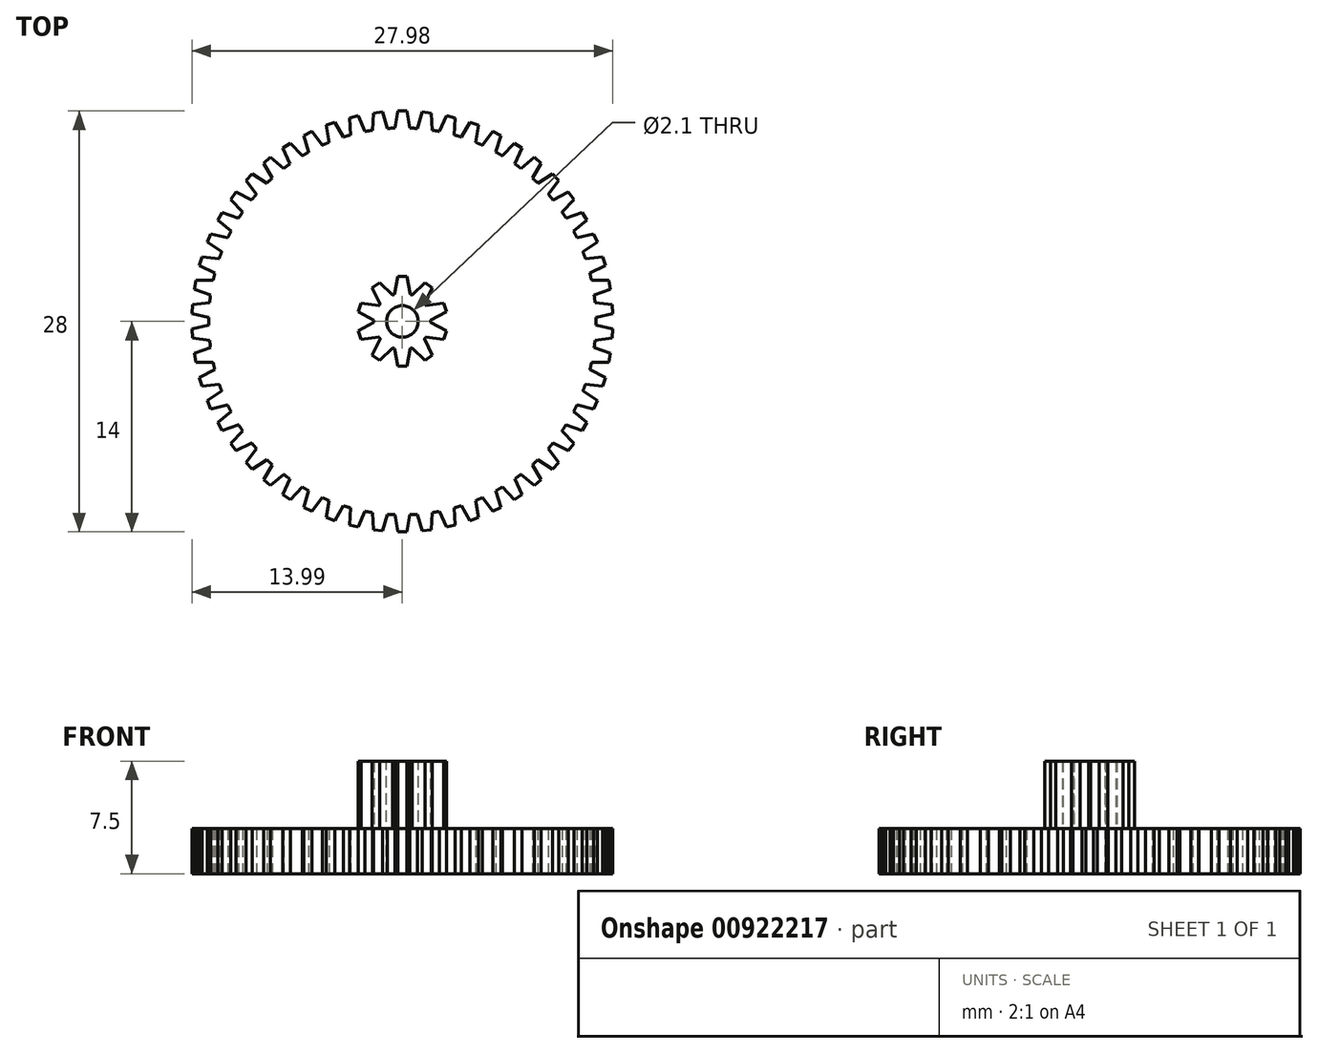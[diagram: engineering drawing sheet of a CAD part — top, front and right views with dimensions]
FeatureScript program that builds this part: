
annotation { "Feature Type Name" : "Feature", "Feature Type Description" : "" }
export const myFeature = defineFeature(function(context is Context, id is Id, definition is map)
    precondition{}
    {
        {
            var Q0;
            Q0=qCreatedBy(makeId("Top.planeOp"),FACE);
            var sketch = newSketch(context, id + "F0", { "sketchPlane" : qUnion([Q0])});
            skCircle(sketch, "E0", {"center": v(0, 0) * mm, "radius": 13.5 * mm, "construction": true});
            skCircle(sketch, "E1", {"center": v(0, 0) * mm, "radius": 14 * mm, "construction": true});
            skCircle(sketch, "E2", {"center": v(0, 0) * mm, "radius": 12.88 * mm});
            skLineSegment(sketch, "E3", {"start": v(0, 12.88) * mm, "end": v(0.5, 12.88) * mm, "construction": true});
            skLineSegment(sketch, "E4", {"start": v(0, 12.88) * mm, "end": v(-0.5, 12.88) * mm, "construction": true});
            skLineSegment(sketch, "E5", {"start": v(-1.53, 7.02) * mm, "end": v(-0.5, 12.87) * mm, "construction": true});
            skLineSegment(sketch, "E6", {"start": v(1.53, 7.03) * mm, "end": v(0.3, 14) * mm, "construction": true});
            skLineSegment(sketch, "E7", {"start": v(-1.53, 7.03) * mm, "end": v(-0.3, 14) * mm});
            skLineSegment(sketch, "E8", {"start": v(0.3, 14) * mm, "end": v(-0.3, 14) * mm});
            skLineSegment(sketch, "E9", {"start": v(0.3, 14) * mm, "end": v(0.5, 12.87) * mm});
            skLineSegment(sketch, "E10.1.0", {"start": v(-2.34, 6.8) * mm, "end": v(-1.93, 13.87) * mm});
            skLineSegment(sketch, "E10.1.1", {"start": v(-1.32, 13.94) * mm, "end": v(-1.93, 13.87) * mm});
            skLineSegment(sketch, "E10.1.2", {"start": v(-1.32, 13.94) * mm, "end": v(-1, 12.84) * mm});
            skLineSegment(sketch, "E10.2.0", {"start": v(-3.11, 6.5) * mm, "end": v(-3.52, 13.55) * mm});
            skLineSegment(sketch, "E10.2.1", {"start": v(-2.93, 13.69) * mm, "end": v(-3.52, 13.55) * mm});
            skLineSegment(sketch, "E10.2.2", {"start": v(-2.93, 13.69) * mm, "end": v(-2.48, 12.63) * mm});
            skLineSegment(sketch, "E11.1.3.0", {"start": v(-3.84, 6.09) * mm, "end": v(-5.07, 13.05) * mm});
            skLineSegment(sketch, "E11.3.3.0", {"start": v(-4.5, 13.26) * mm, "end": v(-5.07, 13.05) * mm});
            skLineSegment(sketch, "E11.6.3.0", {"start": v(-4.5, 13.26) * mm, "end": v(-3.93, 12.26) * mm});
            skLineSegment(sketch, "E11.1.4.0", {"start": v(-4.52, 5.6) * mm, "end": v(-6.55, 12.37) * mm});
            skLineSegment(sketch, "E11.3.4.0", {"start": v(-6.01, 12.64) * mm, "end": v(-6.55, 12.37) * mm});
            skLineSegment(sketch, "E11.6.4.0", {"start": v(-6.01, 12.64) * mm, "end": v(-5.33, 11.72) * mm});
            skLineSegment(sketch, "E11.1.5.0", {"start": v(-5.14, 5.04) * mm, "end": v(-7.94, 11.53) * mm});
            skLineSegment(sketch, "E11.3.5.0", {"start": v(-7.44, 11.86) * mm, "end": v(-7.94, 11.53) * mm});
            skLineSegment(sketch, "E11.6.5.0", {"start": v(-7.44, 11.86) * mm, "end": v(-6.65, 11.02) * mm});
            skLineSegment(sketch, "E11.1.6.0", {"start": v(-5.7, 4.4) * mm, "end": v(-9.23, 10.53) * mm});
            skLineSegment(sketch, "E11.3.6.0", {"start": v(-8.77, 10.92) * mm, "end": v(-9.23, 10.53) * mm});
            skLineSegment(sketch, "E11.6.6.0", {"start": v(-8.77, 10.92) * mm, "end": v(-7.89, 10.18) * mm});
            skLineSegment(sketch, "E11.1.7.0", {"start": v(-6.17, 3.71) * mm, "end": v(-10.39, 9.39) * mm});
            skLineSegment(sketch, "E11.3.7.0", {"start": v(-9.97, 9.82) * mm, "end": v(-10.39, 9.39) * mm});
            skLineSegment(sketch, "E11.6.7.0", {"start": v(-9.97, 9.82) * mm, "end": v(-9.01, 9.2) * mm});
            skLineSegment(sketch, "E11.1.8.0", {"start": v(-6.56, 2.97) * mm, "end": v(-11.4, 8.12) * mm});
            skLineSegment(sketch, "E11.3.8.0", {"start": v(-11.05, 8.6) * mm, "end": v(-11.4, 8.12) * mm});
            skLineSegment(sketch, "E11.6.8.0", {"start": v(-11.05, 8.6) * mm, "end": v(-10.02, 8.09) * mm});
            skLineSegment(sketch, "E11.1.9.0", {"start": v(-6.86, 2.2) * mm, "end": v(-12.27, 6.74) * mm});
            skLineSegment(sketch, "E11.3.9.0", {"start": v(-11.97, 7.26) * mm, "end": v(-12.27, 6.74) * mm});
            skLineSegment(sketch, "E11.6.9.0", {"start": v(-11.97, 7.26) * mm, "end": v(-10.9, 6.87) * mm});
            skLineSegment(sketch, "E11.1.10.0", {"start": v(-7.06, 1.38) * mm, "end": v(-12.97, 5.27) * mm});
            skLineSegment(sketch, "E11.3.10.0", {"start": v(-12.73, 5.82) * mm, "end": v(-12.97, 5.27) * mm});
            skLineSegment(sketch, "E11.6.10.0", {"start": v(-12.73, 5.82) * mm, "end": v(-11.61, 5.56) * mm});
            skLineSegment(sketch, "E11.1.11.0", {"start": v(-7.18, 0.55) * mm, "end": v(-13.5, 3.72) * mm});
            skLineSegment(sketch, "E11.3.11.0", {"start": v(-13.32, 4.3) * mm, "end": v(-13.5, 3.72) * mm});
            skLineSegment(sketch, "E11.6.11.0", {"start": v(-13.32, 4.3) * mm, "end": v(-12.18, 4.17) * mm});
            skLineSegment(sketch, "E11.1.12.0", {"start": v(-7.2, -0.29) * mm, "end": v(-13.84, 2.13) * mm});
            skLineSegment(sketch, "E11.3.12.0", {"start": v(-13.73, 2.73) * mm, "end": v(-13.84, 2.13) * mm});
            skLineSegment(sketch, "E11.6.12.0", {"start": v(-13.73, 2.73) * mm, "end": v(-12.58, 2.73) * mm});
            skLineSegment(sketch, "E11.1.13.0", {"start": v(-7.11, -1.12) * mm, "end": v(-14, 0.51) * mm});
            skLineSegment(sketch, "E11.3.13.0", {"start": v(-13.96, 1.12) * mm, "end": v(-14, 0.51) * mm});
            skLineSegment(sketch, "E11.6.13.0", {"start": v(-13.96, 1.12) * mm, "end": v(-12.81, 1.25) * mm});
            skLineSegment(sketch, "E11.1.14.0", {"start": v(-6.93, -1.94) * mm, "end": v(-13.96, -1.12) * mm});
            skLineSegment(sketch, "E11.3.14.0", {"start": v(-14, -0.51) * mm, "end": v(-13.96, -1.12) * mm});
            skLineSegment(sketch, "E11.6.14.0", {"start": v(-14, -0.51) * mm, "end": v(-12.87, -0.25) * mm});
            skLineSegment(sketch, "E11.1.15.0", {"start": v(-6.66, -2.73) * mm, "end": v(-13.73, -2.73) * mm});
            skLineSegment(sketch, "E11.3.15.0", {"start": v(-13.84, -2.13) * mm, "end": v(-13.73, -2.73) * mm});
            skLineSegment(sketch, "E11.6.15.0", {"start": v(-13.84, -2.13) * mm, "end": v(-12.76, -1.74) * mm});
            skLineSegment(sketch, "E11.1.16.0", {"start": v(-6.3, -3.48) * mm, "end": v(-13.32, -4.3) * mm});
            skLineSegment(sketch, "E11.3.16.0", {"start": v(-13.5, -3.72) * mm, "end": v(-13.32, -4.3) * mm});
            skLineSegment(sketch, "E11.6.16.0", {"start": v(-13.5, -3.72) * mm, "end": v(-12.47, -3.2) * mm});
            skLineSegment(sketch, "E11.1.17.0", {"start": v(-5.85, -4.2) * mm, "end": v(-12.73, -5.82) * mm});
            skLineSegment(sketch, "E11.3.17.0", {"start": v(-12.97, -5.27) * mm, "end": v(-12.73, -5.82) * mm});
            skLineSegment(sketch, "E11.6.17.0", {"start": v(-12.97, -5.27) * mm, "end": v(-12.01, -4.63) * mm});
            skLineSegment(sketch, "E11.1.18.0", {"start": v(-5.33, -4.84) * mm, "end": v(-11.97, -7.26) * mm});
            skLineSegment(sketch, "E11.3.18.0", {"start": v(-12.27, -6.74) * mm, "end": v(-11.97, -7.26) * mm});
            skLineSegment(sketch, "E11.6.18.0", {"start": v(-12.27, -6.74) * mm, "end": v(-11.4, -6) * mm});
            skLineSegment(sketch, "E11.1.19.0", {"start": v(-4.73, -5.43) * mm, "end": v(-11.05, -8.6) * mm});
            skLineSegment(sketch, "E11.3.19.0", {"start": v(-11.4, -8.12) * mm, "end": v(-11.05, -8.6) * mm});
            skLineSegment(sketch, "E11.6.19.0", {"start": v(-11.4, -8.12) * mm, "end": v(-10.62, -7.28) * mm});
            skLineSegment(sketch, "E11.1.20.0", {"start": v(-4.07, -5.94) * mm, "end": v(-9.97, -9.82) * mm});
            skLineSegment(sketch, "E11.3.20.0", {"start": v(-10.39, -9.39) * mm, "end": v(-9.97, -9.82) * mm});
            skLineSegment(sketch, "E11.6.20.0", {"start": v(-10.39, -9.39) * mm, "end": v(-9.7, -8.46) * mm});
            skLineSegment(sketch, "E11.1.21.0", {"start": v(-3.35, -6.37) * mm, "end": v(-8.77, -10.92) * mm});
            skLineSegment(sketch, "E11.3.21.0", {"start": v(-9.23, -10.53) * mm, "end": v(-8.77, -10.92) * mm});
            skLineSegment(sketch, "E11.6.21.0", {"start": v(-9.23, -10.53) * mm, "end": v(-8.65, -9.53) * mm});
            skLineSegment(sketch, "E11.1.22.0", {"start": v(-2.59, -6.72) * mm, "end": v(-7.44, -11.86) * mm});
            skLineSegment(sketch, "E11.3.22.0", {"start": v(-7.94, -11.53) * mm, "end": v(-7.44, -11.86) * mm});
            skLineSegment(sketch, "E11.6.22.0", {"start": v(-7.94, -11.53) * mm, "end": v(-7.49, -10.47) * mm});
            skLineSegment(sketch, "E11.1.23.0", {"start": v(-1.79, -6.97) * mm, "end": v(-6.01, -12.64) * mm});
            skLineSegment(sketch, "E11.3.23.0", {"start": v(-6.55, -12.37) * mm, "end": v(-6.01, -12.64) * mm});
            skLineSegment(sketch, "E11.6.23.0", {"start": v(-6.55, -12.37) * mm, "end": v(-6.22, -11.27) * mm});
            skLineSegment(sketch, "E11.1.24.0", {"start": v(-0.97, -7.13) * mm, "end": v(-4.5, -13.26) * mm});
            skLineSegment(sketch, "E11.3.24.0", {"start": v(-5.07, -13.05) * mm, "end": v(-4.5, -13.26) * mm});
            skLineSegment(sketch, "E11.6.24.0", {"start": v(-5.07, -13.05) * mm, "end": v(-4.87, -11.92) * mm});
            skLineSegment(sketch, "E11.1.25.0", {"start": v(-0.13, -7.2) * mm, "end": v(-2.93, -13.69) * mm});
            skLineSegment(sketch, "E11.3.25.0", {"start": v(-3.52, -13.55) * mm, "end": v(-2.93, -13.69) * mm});
            skLineSegment(sketch, "E11.6.25.0", {"start": v(-3.52, -13.55) * mm, "end": v(-3.46, -12.4) * mm});
            skLineSegment(sketch, "E11.1.26.0", {"start": v(0.7, -7.16) * mm, "end": v(-1.32, -13.94) * mm});
            skLineSegment(sketch, "E11.3.26.0", {"start": v(-1.93, -13.87) * mm, "end": v(-1.32, -13.94) * mm});
            skLineSegment(sketch, "E11.6.26.0", {"start": v(-1.93, -13.87) * mm, "end": v(-2, -12.72) * mm});
            skLineSegment(sketch, "E11.1.27.0", {"start": v(1.53, -7.03) * mm, "end": v(0.3, -14) * mm});
            skLineSegment(sketch, "E11.3.27.0", {"start": v(-0.3, -14) * mm, "end": v(0.3, -14) * mm});
            skLineSegment(sketch, "E11.6.27.0", {"start": v(-0.3, -14) * mm, "end": v(-0.5, -12.87) * mm});
            skLineSegment(sketch, "E11.1.28.0", {"start": v(2.34, -6.8) * mm, "end": v(1.93, -13.87) * mm});
            skLineSegment(sketch, "E11.3.28.0", {"start": v(1.32, -13.94) * mm, "end": v(1.93, -13.87) * mm});
            skLineSegment(sketch, "E11.6.28.0", {"start": v(1.32, -13.94) * mm, "end": v(1, -12.84) * mm});
            skLineSegment(sketch, "E11.1.29.0", {"start": v(3.11, -6.5) * mm, "end": v(3.52, -13.55) * mm});
            skLineSegment(sketch, "E11.3.29.0", {"start": v(2.93, -13.69) * mm, "end": v(3.52, -13.55) * mm});
            skLineSegment(sketch, "E11.6.29.0", {"start": v(2.93, -13.69) * mm, "end": v(2.48, -12.63) * mm});
            skLineSegment(sketch, "E12.1.30.0", {"start": v(3.84, -6.09) * mm, "end": v(5.07, -13.05) * mm});
            skLineSegment(sketch, "E12.3.30.0", {"start": v(4.5, -13.26) * mm, "end": v(5.07, -13.05) * mm});
            skLineSegment(sketch, "E12.6.30.0", {"start": v(4.5, -13.26) * mm, "end": v(3.93, -12.26) * mm});
            skLineSegment(sketch, "E12.1.31.0", {"start": v(4.52, -5.6) * mm, "end": v(6.55, -12.37) * mm});
            skLineSegment(sketch, "E12.3.31.0", {"start": v(6.01, -12.64) * mm, "end": v(6.55, -12.37) * mm});
            skLineSegment(sketch, "E12.6.31.0", {"start": v(6.01, -12.64) * mm, "end": v(5.33, -11.72) * mm});
            skLineSegment(sketch, "E12.1.32.0", {"start": v(5.14, -5.04) * mm, "end": v(7.94, -11.53) * mm});
            skLineSegment(sketch, "E12.3.32.0", {"start": v(7.44, -11.86) * mm, "end": v(7.94, -11.53) * mm});
            skLineSegment(sketch, "E12.6.32.0", {"start": v(7.44, -11.86) * mm, "end": v(6.65, -11.02) * mm});
            skLineSegment(sketch, "E12.1.33.0", {"start": v(5.7, -4.4) * mm, "end": v(9.23, -10.53) * mm});
            skLineSegment(sketch, "E12.3.33.0", {"start": v(8.77, -10.92) * mm, "end": v(9.23, -10.53) * mm});
            skLineSegment(sketch, "E12.6.33.0", {"start": v(8.77, -10.92) * mm, "end": v(7.89, -10.18) * mm});
            skLineSegment(sketch, "E12.1.34.0", {"start": v(6.17, -3.71) * mm, "end": v(10.39, -9.39) * mm});
            skLineSegment(sketch, "E12.3.34.0", {"start": v(9.97, -9.82) * mm, "end": v(10.39, -9.39) * mm});
            skLineSegment(sketch, "E12.6.34.0", {"start": v(9.97, -9.82) * mm, "end": v(9.01, -9.2) * mm});
            skLineSegment(sketch, "E12.1.35.0", {"start": v(6.56, -2.97) * mm, "end": v(11.4, -8.12) * mm});
            skLineSegment(sketch, "E12.3.35.0", {"start": v(11.05, -8.6) * mm, "end": v(11.4, -8.12) * mm});
            skLineSegment(sketch, "E12.6.35.0", {"start": v(11.05, -8.6) * mm, "end": v(10.02, -8.09) * mm});
            skLineSegment(sketch, "E12.1.36.0", {"start": v(6.86, -2.2) * mm, "end": v(12.27, -6.74) * mm});
            skLineSegment(sketch, "E12.3.36.0", {"start": v(11.97, -7.26) * mm, "end": v(12.27, -6.74) * mm});
            skLineSegment(sketch, "E12.6.36.0", {"start": v(11.97, -7.26) * mm, "end": v(10.9, -6.87) * mm});
            skLineSegment(sketch, "E12.1.37.0", {"start": v(7.06, -1.38) * mm, "end": v(12.97, -5.27) * mm});
            skLineSegment(sketch, "E12.3.37.0", {"start": v(12.73, -5.82) * mm, "end": v(12.97, -5.27) * mm});
            skLineSegment(sketch, "E12.6.37.0", {"start": v(12.73, -5.82) * mm, "end": v(11.61, -5.56) * mm});
            skLineSegment(sketch, "E12.1.38.0", {"start": v(7.18, -0.55) * mm, "end": v(13.5, -3.72) * mm});
            skLineSegment(sketch, "E12.3.38.0", {"start": v(13.32, -4.3) * mm, "end": v(13.5, -3.72) * mm});
            skLineSegment(sketch, "E12.6.38.0", {"start": v(13.32, -4.3) * mm, "end": v(12.18, -4.17) * mm});
            skLineSegment(sketch, "E12.1.39.0", {"start": v(7.2, 0.29) * mm, "end": v(13.84, -2.13) * mm});
            skLineSegment(sketch, "E12.3.39.0", {"start": v(13.73, -2.73) * mm, "end": v(13.84, -2.13) * mm});
            skLineSegment(sketch, "E12.6.39.0", {"start": v(13.73, -2.73) * mm, "end": v(12.58, -2.73) * mm});
            skLineSegment(sketch, "E12.1.40.0", {"start": v(7.11, 1.12) * mm, "end": v(14, -0.51) * mm});
            skLineSegment(sketch, "E12.3.40.0", {"start": v(13.96, -1.12) * mm, "end": v(14, -0.51) * mm});
            skLineSegment(sketch, "E12.6.40.0", {"start": v(13.96, -1.12) * mm, "end": v(12.81, -1.25) * mm});
            skLineSegment(sketch, "E12.1.41.0", {"start": v(6.93, 1.94) * mm, "end": v(13.96, 1.12) * mm});
            skLineSegment(sketch, "E12.3.41.0", {"start": v(14, 0.51) * mm, "end": v(13.96, 1.12) * mm});
            skLineSegment(sketch, "E12.6.41.0", {"start": v(14, 0.51) * mm, "end": v(12.87, 0.25) * mm});
            skLineSegment(sketch, "E13.1.42.0", {"start": v(6.66, 2.73) * mm, "end": v(13.73, 2.73) * mm});
            skLineSegment(sketch, "E13.3.42.0", {"start": v(13.84, 2.13) * mm, "end": v(13.73, 2.73) * mm});
            skLineSegment(sketch, "E13.6.42.0", {"start": v(13.84, 2.13) * mm, "end": v(12.76, 1.74) * mm});
            skLineSegment(sketch, "E13.1.43.0", {"start": v(6.3, 3.48) * mm, "end": v(13.32, 4.3) * mm});
            skLineSegment(sketch, "E13.3.43.0", {"start": v(13.5, 3.72) * mm, "end": v(13.32, 4.3) * mm});
            skLineSegment(sketch, "E13.6.43.0", {"start": v(13.5, 3.72) * mm, "end": v(12.47, 3.2) * mm});
            skLineSegment(sketch, "E13.1.44.0", {"start": v(5.85, 4.2) * mm, "end": v(12.73, 5.82) * mm});
            skLineSegment(sketch, "E13.3.44.0", {"start": v(12.97, 5.27) * mm, "end": v(12.73, 5.82) * mm});
            skLineSegment(sketch, "E13.6.44.0", {"start": v(12.97, 5.27) * mm, "end": v(12.01, 4.63) * mm});
            skLineSegment(sketch, "E13.1.45.0", {"start": v(5.33, 4.84) * mm, "end": v(11.97, 7.26) * mm});
            skLineSegment(sketch, "E13.3.45.0", {"start": v(12.27, 6.74) * mm, "end": v(11.97, 7.26) * mm});
            skLineSegment(sketch, "E13.6.45.0", {"start": v(12.27, 6.74) * mm, "end": v(11.4, 6) * mm});
            skLineSegment(sketch, "E13.1.46.0", {"start": v(4.73, 5.43) * mm, "end": v(11.05, 8.6) * mm});
            skLineSegment(sketch, "E13.3.46.0", {"start": v(11.4, 8.12) * mm, "end": v(11.05, 8.6) * mm});
            skLineSegment(sketch, "E13.6.46.0", {"start": v(11.4, 8.12) * mm, "end": v(10.62, 7.28) * mm});
            skLineSegment(sketch, "E13.1.47.0", {"start": v(4.07, 5.94) * mm, "end": v(9.97, 9.82) * mm});
            skLineSegment(sketch, "E13.3.47.0", {"start": v(10.39, 9.39) * mm, "end": v(9.97, 9.82) * mm});
            skLineSegment(sketch, "E13.6.47.0", {"start": v(10.39, 9.39) * mm, "end": v(9.7, 8.46) * mm});
            skLineSegment(sketch, "E14.1.48.0", {"start": v(3.35, 6.37) * mm, "end": v(8.77, 10.92) * mm});
            skLineSegment(sketch, "E14.3.48.0", {"start": v(9.23, 10.53) * mm, "end": v(8.77, 10.92) * mm});
            skLineSegment(sketch, "E14.6.48.0", {"start": v(9.23, 10.53) * mm, "end": v(8.65, 9.53) * mm});
            skLineSegment(sketch, "E14.1.49.0", {"start": v(2.59, 6.72) * mm, "end": v(7.44, 11.86) * mm});
            skLineSegment(sketch, "E14.3.49.0", {"start": v(7.94, 11.53) * mm, "end": v(7.44, 11.86) * mm});
            skLineSegment(sketch, "E14.6.49.0", {"start": v(7.94, 11.53) * mm, "end": v(7.49, 10.47) * mm});
            skLineSegment(sketch, "E14.1.50.0", {"start": v(1.79, 6.97) * mm, "end": v(6.01, 12.64) * mm});
            skLineSegment(sketch, "E14.3.50.0", {"start": v(6.55, 12.37) * mm, "end": v(6.01, 12.64) * mm});
            skLineSegment(sketch, "E14.6.50.0", {"start": v(6.55, 12.37) * mm, "end": v(6.22, 11.27) * mm});
            skLineSegment(sketch, "E14.1.51.0", {"start": v(0.97, 7.13) * mm, "end": v(4.5, 13.26) * mm});
            skLineSegment(sketch, "E14.3.51.0", {"start": v(5.07, 13.05) * mm, "end": v(4.5, 13.26) * mm});
            skLineSegment(sketch, "E14.6.51.0", {"start": v(5.07, 13.05) * mm, "end": v(4.87, 11.92) * mm});
            skLineSegment(sketch, "E14.1.52.0", {"start": v(0.13, 7.2) * mm, "end": v(2.93, 13.69) * mm});
            skLineSegment(sketch, "E14.3.52.0", {"start": v(3.52, 13.55) * mm, "end": v(2.93, 13.69) * mm});
            skLineSegment(sketch, "E14.6.52.0", {"start": v(3.52, 13.55) * mm, "end": v(3.46, 12.4) * mm});
            skLineSegment(sketch, "E14.1.53.0", {"start": v(-0.7, 7.16) * mm, "end": v(1.32, 13.94) * mm});
            skLineSegment(sketch, "E14.3.53.0", {"start": v(1.93, 13.87) * mm, "end": v(1.32, 13.94) * mm});
            skLineSegment(sketch, "E14.6.53.0", {"start": v(1.93, 13.87) * mm, "end": v(2, 12.72) * mm});
            skSolve(sketch);
        }
        {
            var Q0;
            Q0=qSketchRegion(id+"F0",true);
            extrude(context, id + "F1", {"entities" : qUnion([Q0]), "depth" : 3 * mm, "offsetDistance" : 25 * mm});
        }
        {
            var Q0;
            Q0=makeQuery(id+"F1.opExtrude","CAP_FACE",FACE,{"disambiguationData":[OSD([sQuery(id+"F0.wireOp",EDGE,"E2"),sQuery(id+"F0.wireOp",EDGE,"E7"),sQuery(id+"F0.wireOp",EDGE,"E8"),sQuery(id+"F0.wireOp",EDGE,"E9"),sQuery(id+"F0.wireOp",EDGE,"E10.1.0"),sQuery(id+"F0.wireOp",EDGE,"E10.1.1"),sQuery(id+"F0.wireOp",EDGE,"E10.1.2"),sQuery(id+"F0.wireOp",EDGE,"E10.2.0"),sQuery(id+"F0.wireOp",EDGE,"E10.2.1"),sQuery(id+"F0.wireOp",EDGE,"E10.2.2"),sQuery(id+"F0.wireOp",EDGE,"E11.1.3.0"),sQuery(id+"F0.wireOp",EDGE,"E11.3.3.0"),sQuery(id+"F0.wireOp",EDGE,"E11.6.3.0"),sQuery(id+"F0.wireOp",EDGE,"E11.1.4.0"),sQuery(id+"F0.wireOp",EDGE,"E11.3.4.0"),sQuery(id+"F0.wireOp",EDGE,"E11.6.4.0"),sQuery(id+"F0.wireOp",EDGE,"E11.1.5.0"),sQuery(id+"F0.wireOp",EDGE,"E11.3.5.0"),sQuery(id+"F0.wireOp",EDGE,"E11.6.5.0"),sQuery(id+"F0.wireOp",EDGE,"E11.1.6.0"),sQuery(id+"F0.wireOp",EDGE,"E11.3.6.0"),sQuery(id+"F0.wireOp",EDGE,"E11.6.6.0"),sQuery(id+"F0.wireOp",EDGE,"E11.1.7.0"),sQuery(id+"F0.wireOp",EDGE,"E11.3.7.0"),sQuery(id+"F0.wireOp",EDGE,"E11.6.7.0"),sQuery(id+"F0.wireOp",EDGE,"E11.1.8.0"),sQuery(id+"F0.wireOp",EDGE,"E11.3.8.0"),sQuery(id+"F0.wireOp",EDGE,"E11.6.8.0"),sQuery(id+"F0.wireOp",EDGE,"E11.1.9.0"),sQuery(id+"F0.wireOp",EDGE,"E11.3.9.0"),sQuery(id+"F0.wireOp",EDGE,"E11.6.9.0"),sQuery(id+"F0.wireOp",EDGE,"E11.1.10.0"),sQuery(id+"F0.wireOp",EDGE,"E11.3.10.0"),sQuery(id+"F0.wireOp",EDGE,"E11.6.10.0"),sQuery(id+"F0.wireOp",EDGE,"E11.1.11.0"),sQuery(id+"F0.wireOp",EDGE,"E11.3.11.0"),sQuery(id+"F0.wireOp",EDGE,"E11.6.11.0"),sQuery(id+"F0.wireOp",EDGE,"E11.1.12.0"),sQuery(id+"F0.wireOp",EDGE,"E11.3.12.0"),sQuery(id+"F0.wireOp",EDGE,"E11.6.12.0"),sQuery(id+"F0.wireOp",EDGE,"E11.1.13.0"),sQuery(id+"F0.wireOp",EDGE,"E11.3.13.0"),sQuery(id+"F0.wireOp",EDGE,"E11.6.13.0"),sQuery(id+"F0.wireOp",EDGE,"E11.1.14.0"),sQuery(id+"F0.wireOp",EDGE,"E11.3.14.0"),sQuery(id+"F0.wireOp",EDGE,"E11.6.14.0"),sQuery(id+"F0.wireOp",EDGE,"E11.1.15.0"),sQuery(id+"F0.wireOp",EDGE,"E11.3.15.0"),sQuery(id+"F0.wireOp",EDGE,"E11.6.15.0"),sQuery(id+"F0.wireOp",EDGE,"E11.1.16.0"),sQuery(id+"F0.wireOp",EDGE,"E11.3.16.0"),sQuery(id+"F0.wireOp",EDGE,"E11.6.16.0"),sQuery(id+"F0.wireOp",EDGE,"E11.1.17.0"),sQuery(id+"F0.wireOp",EDGE,"E11.3.17.0"),sQuery(id+"F0.wireOp",EDGE,"E11.6.17.0"),sQuery(id+"F0.wireOp",EDGE,"E11.1.18.0"),sQuery(id+"F0.wireOp",EDGE,"E11.3.18.0"),sQuery(id+"F0.wireOp",EDGE,"E11.6.18.0"),sQuery(id+"F0.wireOp",EDGE,"E11.1.19.0"),sQuery(id+"F0.wireOp",EDGE,"E11.3.19.0"),sQuery(id+"F0.wireOp",EDGE,"E11.6.19.0"),sQuery(id+"F0.wireOp",EDGE,"E11.1.20.0"),sQuery(id+"F0.wireOp",EDGE,"E11.3.20.0"),sQuery(id+"F0.wireOp",EDGE,"E11.6.20.0"),sQuery(id+"F0.wireOp",EDGE,"E11.1.21.0"),sQuery(id+"F0.wireOp",EDGE,"E11.3.21.0"),sQuery(id+"F0.wireOp",EDGE,"E11.6.21.0"),sQuery(id+"F0.wireOp",EDGE,"E11.1.22.0"),sQuery(id+"F0.wireOp",EDGE,"E11.3.22.0"),sQuery(id+"F0.wireOp",EDGE,"E11.6.22.0"),sQuery(id+"F0.wireOp",EDGE,"E11.1.23.0"),sQuery(id+"F0.wireOp",EDGE,"E11.3.23.0"),sQuery(id+"F0.wireOp",EDGE,"E11.6.23.0"),sQuery(id+"F0.wireOp",EDGE,"E11.1.24.0"),sQuery(id+"F0.wireOp",EDGE,"E11.3.24.0"),sQuery(id+"F0.wireOp",EDGE,"E11.6.24.0"),sQuery(id+"F0.wireOp",EDGE,"E11.1.25.0"),sQuery(id+"F0.wireOp",EDGE,"E11.3.25.0"),sQuery(id+"F0.wireOp",EDGE,"E11.6.25.0"),sQuery(id+"F0.wireOp",EDGE,"E11.1.26.0"),sQuery(id+"F0.wireOp",EDGE,"E11.3.26.0"),sQuery(id+"F0.wireOp",EDGE,"E11.6.26.0"),sQuery(id+"F0.wireOp",EDGE,"E11.1.27.0"),sQuery(id+"F0.wireOp",EDGE,"E11.3.27.0"),sQuery(id+"F0.wireOp",EDGE,"E11.6.27.0"),sQuery(id+"F0.wireOp",EDGE,"E11.1.28.0"),sQuery(id+"F0.wireOp",EDGE,"E11.3.28.0"),sQuery(id+"F0.wireOp",EDGE,"E11.6.28.0"),sQuery(id+"F0.wireOp",EDGE,"E11.1.29.0"),sQuery(id+"F0.wireOp",EDGE,"E11.3.29.0"),sQuery(id+"F0.wireOp",EDGE,"E11.6.29.0")])],"isStart":false});
            var sketch = newSketch(context, id + "F2", { "sketchPlane" : qUnion([Q0])});
            skCircle(sketch, "E15", {"center": v(0, 0) * mm, "radius": 2.5 * mm, "construction": true});
            skCircle(sketch, "E16", {"center": v(0, 0) * mm, "radius": 3 * mm, "construction": true});
            skCircle(sketch, "E17", {"center": v(0, 0) * mm, "radius": 1.88 * mm});
            skLineSegment(sketch, "E18", {"start": v(0, 1.88) * mm, "end": v(0.5, 1.88) * mm, "construction": true});
            skLineSegment(sketch, "E19", {"start": v(0, 1.88) * mm, "end": v(-0.5, 1.88) * mm, "construction": true});
            skLineSegment(sketch, "E20", {"start": v(-0.51, 1.8) * mm, "end": v(-0.3, 2.98) * mm, "construction": true});
            skLineSegment(sketch, "E21", {"start": v(0.51, 1.8) * mm, "end": v(0.3, 2.98) * mm, "construction": true});
            skLineSegment(sketch, "E22", {"start": v(-0.51, 1.8) * mm, "end": v(-0.3, 2.98) * mm});
            skLineSegment(sketch, "E23", {"start": v(0.3, 2.98) * mm, "end": v(-0.3, 2.98) * mm});
            skLineSegment(sketch, "E24", {"start": v(0.3, 2.98) * mm, "end": v(0.51, 1.8) * mm});
            skLineSegment(sketch, "E25.1.0", {"start": v(-1.47, 1.16) * mm, "end": v(-2, 2.24) * mm});
            skLineSegment(sketch, "E25.1.1", {"start": v(-1.5, 2.6) * mm, "end": v(-2, 2.24) * mm});
            skLineSegment(sketch, "E25.1.2", {"start": v(-1.5, 2.6) * mm, "end": v(-0.65, 1.76) * mm});
            skLineSegment(sketch, "E25.2.0", {"start": v(-1.87, 0.07) * mm, "end": v(-2.93, 0.63) * mm});
            skLineSegment(sketch, "E25.2.1", {"start": v(-2.74, 1.21) * mm, "end": v(-2.93, 0.63) * mm});
            skLineSegment(sketch, "E25.2.2", {"start": v(-2.74, 1.21) * mm, "end": v(-1.56, 1.04) * mm});
            skLineSegment(sketch, "E26.1.3.0", {"start": v(-1.56, -1.04) * mm, "end": v(-2.74, -1.21) * mm});
            skLineSegment(sketch, "E26.3.3.0", {"start": v(-2.93, -0.63) * mm, "end": v(-2.74, -1.21) * mm});
            skLineSegment(sketch, "E26.6.3.0", {"start": v(-2.93, -0.63) * mm, "end": v(-1.87, -0.07) * mm});
            skLineSegment(sketch, "E26.1.4.0", {"start": v(-0.65, -1.76) * mm, "end": v(-1.5, -2.6) * mm});
            skLineSegment(sketch, "E26.3.4.0", {"start": v(-2, -2.24) * mm, "end": v(-1.5, -2.6) * mm});
            skLineSegment(sketch, "E26.6.4.0", {"start": v(-2, -2.24) * mm, "end": v(-1.47, -1.16) * mm});
            skLineSegment(sketch, "E26.1.5.0", {"start": v(0.51, -1.8) * mm, "end": v(0.3, -2.98) * mm});
            skLineSegment(sketch, "E26.3.5.0", {"start": v(-0.3, -2.98) * mm, "end": v(0.3, -2.98) * mm});
            skLineSegment(sketch, "E26.6.5.0", {"start": v(-0.3, -2.98) * mm, "end": v(-0.51, -1.8) * mm});
            skLineSegment(sketch, "E26.1.6.0", {"start": v(1.47, -1.16) * mm, "end": v(2, -2.24) * mm});
            skLineSegment(sketch, "E26.3.6.0", {"start": v(1.5, -2.6) * mm, "end": v(2, -2.24) * mm});
            skLineSegment(sketch, "E26.6.6.0", {"start": v(1.5, -2.6) * mm, "end": v(0.65, -1.76) * mm});
            skLineSegment(sketch, "E26.1.7.0", {"start": v(1.87, -0.07) * mm, "end": v(2.93, -0.63) * mm});
            skLineSegment(sketch, "E26.3.7.0", {"start": v(2.74, -1.21) * mm, "end": v(2.93, -0.63) * mm});
            skLineSegment(sketch, "E26.6.7.0", {"start": v(2.74, -1.21) * mm, "end": v(1.56, -1.04) * mm});
            skLineSegment(sketch, "E26.1.8.0", {"start": v(1.56, 1.04) * mm, "end": v(2.74, 1.21) * mm});
            skLineSegment(sketch, "E26.3.8.0", {"start": v(2.93, 0.63) * mm, "end": v(2.74, 1.21) * mm});
            skLineSegment(sketch, "E26.6.8.0", {"start": v(2.93, 0.63) * mm, "end": v(1.87, 0.07) * mm});
            skLineSegment(sketch, "E26.1.9.0", {"start": v(0.65, 1.76) * mm, "end": v(1.5, 2.6) * mm});
            skLineSegment(sketch, "E26.3.9.0", {"start": v(2, 2.24) * mm, "end": v(1.5, 2.6) * mm});
            skLineSegment(sketch, "E26.6.9.0", {"start": v(2, 2.24) * mm, "end": v(1.47, 1.16) * mm});
            skSolve(sketch);
        }
        {
            var Q0;
            Q0=qSketchRegion(id+"F2",true);
            extrude(context, id + "F3", {"entities" : qUnion([Q0]), "operationType" : NewBodyOperationType.ADD, "depth" : 4.5 * mm, "offsetDistance" : 25 * mm});
        }
        {
            var Q0;
            Q0=makeQuery(id+"F3.opExtrude","CAP_FACE",FACE,{"disambiguationData":[OSD([sQuery(id+"F2.wireOp",EDGE,"E17"),sQuery(id+"F2.wireOp",EDGE,"E22"),sQuery(id+"F2.wireOp",EDGE,"E23"),sQuery(id+"F2.wireOp",EDGE,"E24"),sQuery(id+"F2.wireOp",EDGE,"E25.1.0"),sQuery(id+"F2.wireOp",EDGE,"E25.1.1"),sQuery(id+"F2.wireOp",EDGE,"E25.1.2"),sQuery(id+"F2.wireOp",EDGE,"E25.2.0"),sQuery(id+"F2.wireOp",EDGE,"E25.2.1"),sQuery(id+"F2.wireOp",EDGE,"E25.2.2"),sQuery(id+"F2.wireOp",EDGE,"E26.1.3.0"),sQuery(id+"F2.wireOp",EDGE,"E26.3.3.0"),sQuery(id+"F2.wireOp",EDGE,"E26.6.3.0"),sQuery(id+"F2.wireOp",EDGE,"E26.1.4.0"),sQuery(id+"F2.wireOp",EDGE,"E26.3.4.0"),sQuery(id+"F2.wireOp",EDGE,"E26.6.4.0"),sQuery(id+"F2.wireOp",EDGE,"E26.1.5.0"),sQuery(id+"F2.wireOp",EDGE,"E26.3.5.0"),sQuery(id+"F2.wireOp",EDGE,"E26.6.5.0"),sQuery(id+"F2.wireOp",EDGE,"E26.1.6.0"),sQuery(id+"F2.wireOp",EDGE,"E26.3.6.0"),sQuery(id+"F2.wireOp",EDGE,"E26.6.6.0"),sQuery(id+"F2.wireOp",EDGE,"E26.1.7.0"),sQuery(id+"F2.wireOp",EDGE,"E26.3.7.0"),sQuery(id+"F2.wireOp",EDGE,"E26.6.7.0"),sQuery(id+"F2.wireOp",EDGE,"E26.1.8.0"),sQuery(id+"F2.wireOp",EDGE,"E26.3.8.0"),sQuery(id+"F2.wireOp",EDGE,"E26.6.8.0"),sQuery(id+"F2.wireOp",EDGE,"E26.1.9.0"),sQuery(id+"F2.wireOp",EDGE,"E26.3.9.0"),sQuery(id+"F2.wireOp",EDGE,"E26.6.9.0")])],"isStart":false});
            var sketch = newSketch(context, id + "F4", { "sketchPlane" : qUnion([Q0])});
            skCircle(sketch, "E27", {"center": v(0, 0) * mm, "radius": 1.05 * mm});
            skSolve(sketch);
        }
        {
            var Q0;
            Q0=qSketchRegion(id+"F4",true);
            extrude(context, id + "F5", {"entities" : qUnion([Q0]), "operationType" : NewBodyOperationType.REMOVE, "endBound" : BoundingType.THROUGH_ALL, "oppositeDirection" : true, "depth" : 25 * mm, "offsetDistance" : 25 * mm});
        }
    });
